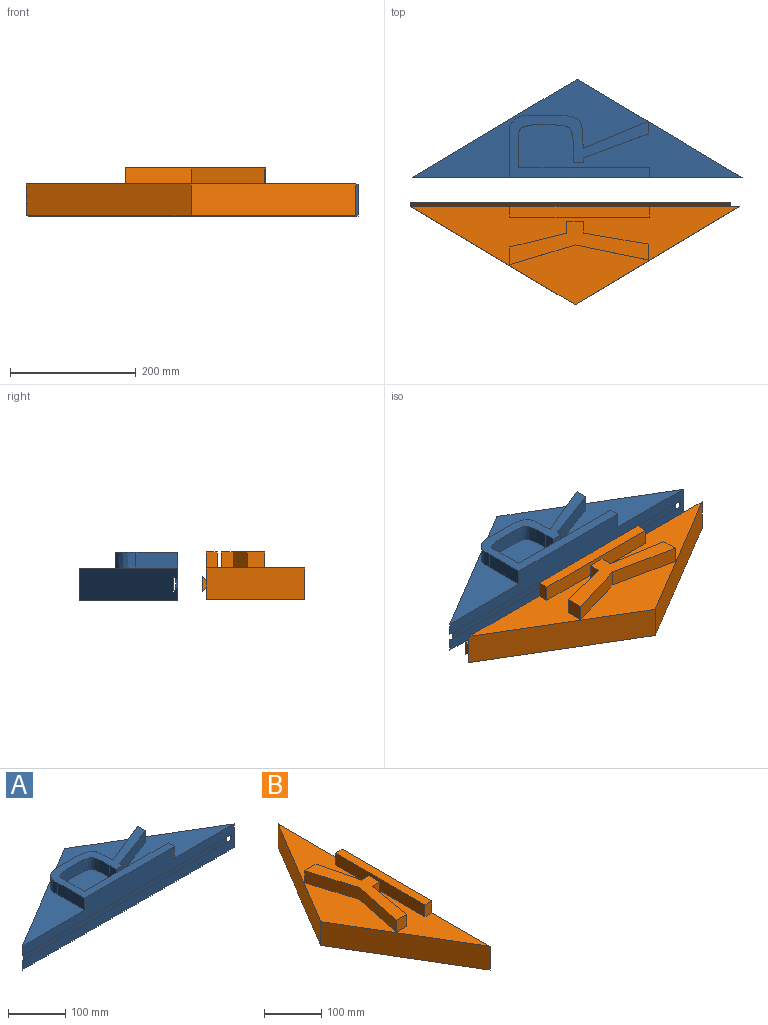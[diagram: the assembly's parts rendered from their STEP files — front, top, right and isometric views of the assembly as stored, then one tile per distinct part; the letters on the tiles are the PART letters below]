
ASSEMBLY  parts=2 mates=1
PART A: 23 faces, bbox 523.5x156.2x76.2 mm
  f0: plane 374.28x156.2mm, normal (0,0,1), area 16029.7mm2, adj f1,f2,f3,f10,f20,f21
  f1: plane 261.74x156.2mm, normal (0.51,0.86,0), area 15334.6mm2, adj f0,f2,f3,f4,f5,f6,f7,f8
  f2: plane 261.74x156.2mm, normal (-0.51,0.86,0), area 15250.7mm2, adj f0,f1,f3,f5,f6,f7,f8
  f3: plane 523.47x76.2mm, normal (0,-1,0), area 26958.3mm2, adj f0,f1,f2,f4,f5,f6,f8,f9
  f4: plane 354.59x89.04mm, normal (0,0,1), area 16056.2mm2, adj f1,f3,f11,f12,f13,f14,f15,f16
  f5: plane 523.47x156.2mm, normal (0,0,-1), area 40882.4mm2, adj f1,f2,f3
  f6: plane 518.22x7.62mm, normal (0,0.75,0.66), area 5191.6mm2, adj f1,f2,f3,f7,f9
  f7: plane 500.95x25.4mm, normal (0,-1,0), area 12724.1mm2, adj f1,f2,f6,f8
  f8: plane 518.22x7.62mm, normal (0,0.75,-0.66), area 5191.6mm2, adj f1,f2,f3,f7,f9
  f9: plane 17.27x3.13mm, normal (-1,0,0), area 43mm2, adj f1,f3,f6,f8
  f10: plane 66.07x25.4mm, normal (-1,0,0), area 1678.2mm2, adj f0,f3,f21,f22
  f11: plane 25.4x15.44mm, normal (1,0,0), area 392.1mm2, adj f3,f4,f12,f22
  f12: plane 207.1x25.4mm, normal (0,1,0), area 5260.3mm2, adj f4,f11,f13,f22
  f13: plane 51.33x25.4mm, normal (1,0,0), area 1303.7mm2, adj f4,f12,f14,f22
  f14: extruded ~86.57x43.45mm, area 3321.5mm2, adj f4,f13,f15,f22
  f15: plane 25.4x17.18mm, normal (-1,0,0), area 436.4mm2, adj f4,f14,f16,f22
  f16: plane 25.4x15.99mm, normal (0,-1,0), area 406.2mm2, adj f4,f15,f17,f22
  f17: plane 25.4x7.63mm, normal (1,0,0), area 193.9mm2, adj f4,f16,f18,f22
  f18: plane 102.55x37.92mm, normal (0.35,-0.94,0), area 2777.1mm2, adj f4,f17,f19,f22
  f19: plane 25.4x19.9mm, normal (1,0,0), area 505.4mm2, adj f4,f18,f20,f22
  f20: plane 102.55x42.43mm, normal (-0.38,0.92,0), area 2819mm2, adj f0,f19,f21,f22
  f21: extruded ~117.37x53.06mm, area 4553.2mm2, adj f0,f10,f20,f22
  f22: plane 222.62x100.29mm, normal (0,0,1), area 8796.4mm2, adj f3,f10,f11,f12,f13,f14,f15,f16
PART B: 25 faces, bbox 162.9x523.9x76.2 mm
  f0: plane 523.47x156.2mm, normal (0,0,1), area 31347.8mm2, adj f1,f2,f3,f5,f6,f7,f9,f10
  f1: plane 261.73x156.2mm, normal (-0.86,0.51,0), area 15483.8mm2, adj f0,f2,f3,f4,f19
  f2: plane 261.73x156.2mm, normal (-0.86,-0.51,0), area 15483.8mm2, adj f0,f1,f3,f4
  f3: plane 523.47x76.2mm, normal (1,0,0), area 27050.3mm2, adj f0,f1,f2,f4,f5,f6,f8,f20
  f4: plane 523.47x156.2mm, normal (0,0,-1), area 40882.7mm2, adj f1,f2,f3
  f5: plane 25.4x17.09mm, normal (0,-1,0), area 434mm2, adj f0,f3,f7,f8
  f6: plane 25.4x17.09mm, normal (0,1,0), area 434mm2, adj f0,f3,f7,f8
  f7: plane 221.49x25.4mm, normal (-1,0,0), area 5625.8mm2, adj f0,f5,f6,f8
  f8: plane 221.49x17.09mm, normal (0,0,1), area 3784.3mm2, adj f3,f5,f6,f7
  f9: plane 25.4x25.26mm, normal (0,-1,0), area 641.5mm2, adj f0,f10,f17,f18
  f10: plane 102.81x25.4mm, normal (0.99,-0.17,0), area 2648.8mm2, adj f0,f9,f11,f18
  f11: plane 25.4x18.67mm, normal (0,-1,0), area 474.3mm2, adj f0,f10,f12,f18
  f12: plane 26.79x25.4mm, normal (1,0,0), area 680.6mm2, adj f0,f11,f13,f18
  f13: plane 25.4x18.67mm, normal (0,1,0), area 474.3mm2, adj f0,f12,f14,f18
  f14: plane 90.25x25.4mm, normal (0.97,0.24,0), area 2359.3mm2, adj f0,f13,f15,f18
  f15: plane 28.28x25.4mm, normal (0,1,0), area 718.4mm2, adj f0,f14,f16,f18
  f16: plane 103.65x31.58mm, normal (-0.96,-0.29,0), area 2752.1mm2, adj f0,f15,f17,f18
  f17: plane 116.21x25.4mm, normal (-0.98,0.2,0), area 3014.2mm2, adj f0,f9,f16,f18
  f18: plane 219.86x68.93mm, normal (0,0,1), area 5750.6mm2, adj f9,f10,f11,f12,f13,f14,f15,f16
  f19: plane 10.17x0.39mm, normal (-1,0,0), area 4mm2, adj f1,f20,f21,f23
  f20: plane 508.51x7.46mm, normal (-0.75,0,0.67), area 5083.4mm2, adj f3,f19,f22,f23,f24
  f21: plane 508.51x7.7mm, normal (-0.76,0,-0.65), area 5176.8mm2, adj f3,f19,f22,f23,f24
  f22: plane 508.51x25.33mm, normal (1,0,0), area 12879.1mm2, adj f20,f21,f23,f24
  f23: plane 25.33x6.66mm, normal (0,1,0), area 118.2mm2, adj f19,f20,f21,f22
  f24: plane 25.33x6.66mm, normal (0,-1,0), area 118.2mm2, adj f3,f20,f21,f22
PLACE A rot(axis=(0,0,1),0deg) t=(95.45,61.17,-21.32)mm
PLACE B rot(axis=(0,0,1),90deg) t=(-164.33,15.45,-21.3)mm
MATE slider B.f22 <-> A.f7  axis (0,1,0) through (-172.21,22.11,4.08)mm
